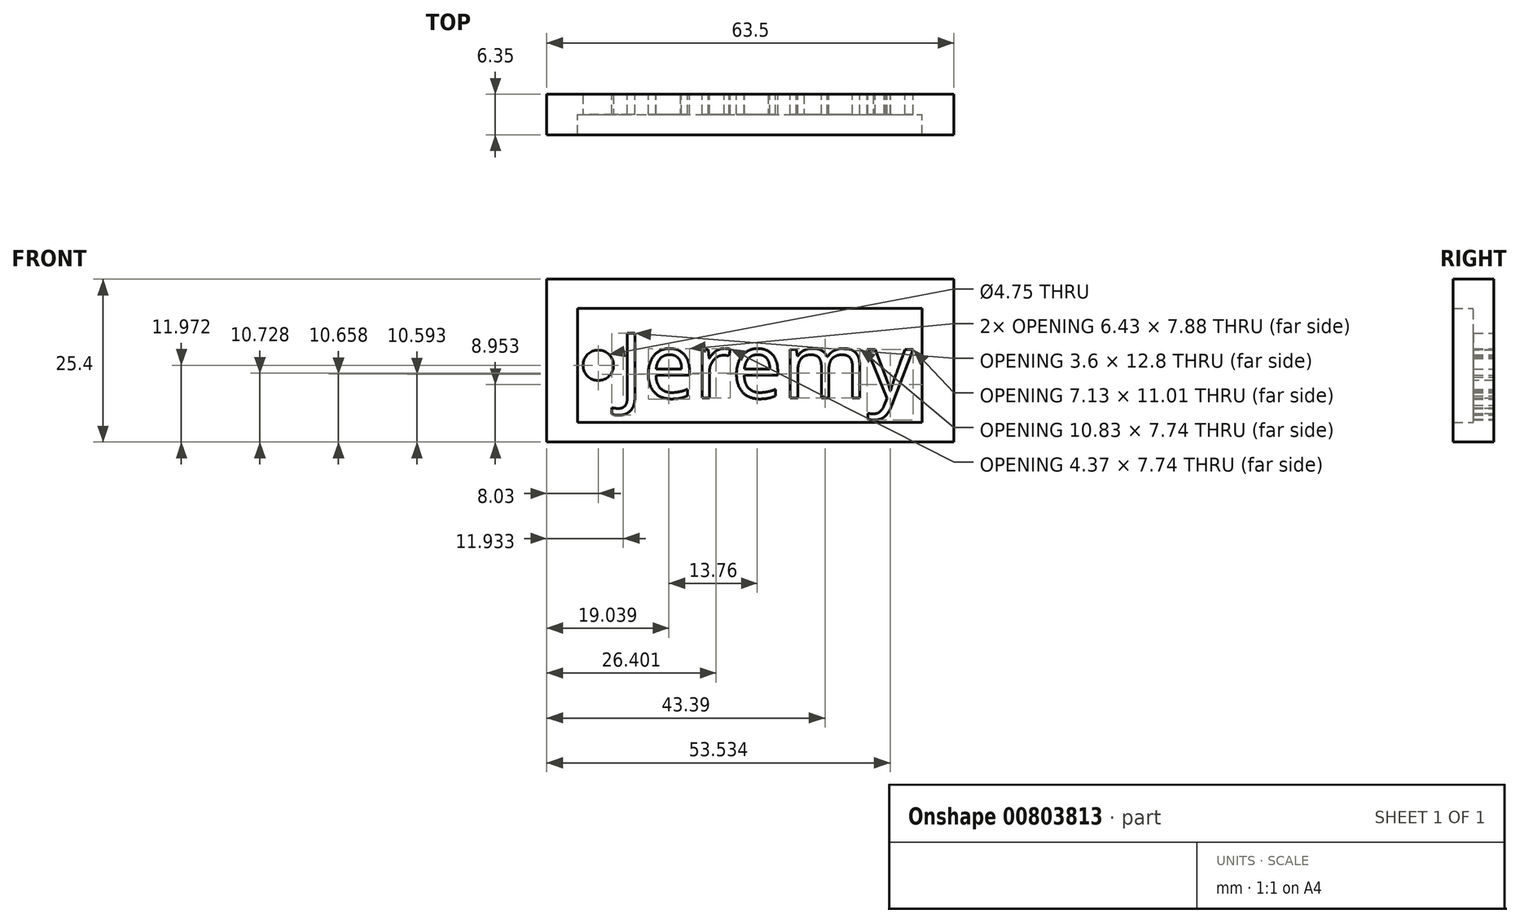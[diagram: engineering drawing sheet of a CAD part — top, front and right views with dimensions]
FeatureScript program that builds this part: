
annotation { "Feature Type Name" : "Feature", "Feature Type Description" : "" }
export const myFeature = defineFeature(function(context is Context, id is Id, definition is map)
    precondition{}
    {
        {
            var Q0;
            Q0=qCreatedBy(makeId("Front.planeOp"),FACE);
            var sketch = newSketch(context, id + "F0", { "sketchPlane" : qUnion([Q0])});
            skLineSegment(sketch, "E0.bottom", {"start": v(0, 0) * mm, "end": v(63.5, 0) * mm});
            skLineSegment(sketch, "E0.top", {"start": v(0, 25.4) * mm, "end": v(63.5, 25.4) * mm});
            skLineSegment(sketch, "E0.left", {"start": v(0, 0) * mm, "end": v(0, 25.4) * mm});
            skLineSegment(sketch, "E0.right", {"start": v(63.5, 0) * mm, "end": v(63.5, 25.4) * mm});
            skLineSegment(sketch, "E1.bottom", {"start": v(4.82, 3.07) * mm, "end": v(58.55, 3.07) * mm});
            skLineSegment(sketch, "E1.top", {"start": v(4.82, 20.88) * mm, "end": v(58.55, 20.88) * mm});
            skLineSegment(sketch, "E1.left", {"start": v(4.82, 3.07) * mm, "end": v(4.82, 20.88) * mm});
            skLineSegment(sketch, "E1.right", {"start": v(58.55, 3.07) * mm, "end": v(58.55, 20.88) * mm});
            skSolve(sketch);
        }
        {
            var Q0;
            Q0=makeQuery(id+"F0.imprint","IMPRINT",FACE,{"disambiguationData":[TD([[makeQuery(id+"F0.imprint","IMPRINT",EDGE,{"derivedFrom":sQuery(id+"F0.wireOp",EDGE,"E0.bottom")}),1.0]])]});
            extrude(context, id + "F1", {"entities" : qUnion([Q0]), "depth" : 6.35 * mm, "offsetDistance" : 25.4 * mm});
        }
        {
            var Q0;
            Q0=makeQuery(id+"F0.imprint","IMPRINT",FACE,{"disambiguationData":[TD([[makeQuery(id+"F0.imprint","IMPRINT",EDGE,{"derivedFrom":sQuery(id+"F0.wireOp",EDGE,"E1.bottom")}),1.0]])]});
            extrude(context, id + "F2", {"entities" : qUnion([Q0]), "operationType" : NewBodyOperationType.ADD, "depth" : 3.17 * mm, "offsetDistance" : 25.4 * mm});
        }
        {
            var Q0;
            Q0=makeQuery(id+"F2.opExtrude","CAP_FACE",FACE,{"disambiguationData":[OSD([sQuery(id+"F0.wireOp",EDGE,"E1.bottom"),sQuery(id+"F0.wireOp",EDGE,"E1.top"),sQuery(id+"F0.wireOp",EDGE,"E1.left"),sQuery(id+"F0.wireOp",EDGE,"E1.right")])],"isStart":false});
            var sketch = newSketch(context, id + "F3", { "sketchPlane" : qUnion([Q0])});
            skCircle(sketch, "E2", {"center": v(8.03, 11.97) * mm, "radius": 2.38 * mm});
            skPoint(sketch, "E2.centerSnap0", {"position": v(4.82, 11.97) * mm});
            skSolve(sketch);
        }
        {
            var Q0;
            Q0=makeQuery(id+"F3.imprint","IMPRINT",FACE,{"disambiguationData":[TD([[makeQuery(id+"F3.imprint","IMPRINT",EDGE,{"derivedFrom":sQuery(id+"F3.wireOp",EDGE,"E2")}),1.0]])]});
            extrude(context, id + "F4", {"entities" : qUnion([Q0]), "operationType" : NewBodyOperationType.REMOVE, "oppositeDirection" : true, "depth" : 3.17 * mm, "offsetDistance" : 25.4 * mm});
        }
        {
            var Q0;
            Q0=makeQuery(id+"F2.opExtrude","CAP_FACE",FACE,{"disambiguationData":[OSD([sQuery(id+"F0.wireOp",EDGE,"E1.bottom"),sQuery(id+"F0.wireOp",EDGE,"E1.top"),sQuery(id+"F0.wireOp",EDGE,"E1.left"),sQuery(id+"F0.wireOp",EDGE,"E1.right")])],"isStart":false});
            var sketch = newSketch(context, id + "F5", { "sketchPlane" : qUnion([Q0])});
            skText(sketch, "E3", { "text": "Jeremy", "fontName": "OpenSans-Regular.ttf"});
            const initialGuessF5  = {"E3": [0.01124, 0.00686, 1, 0, 0.01022]};
            skSetInitialGuess(sketch, initialGuessF5);
            skSolve(sketch);
        }
        {
            var Q0;
            Q0 = qSketchRegion(id + "F5", true);
            extrude(context, id + "F6", {"entities" : qUnion([Q0]), "operationType" : NewBodyOperationType.REMOVE, "depth" : 2.5 * mm, "offsetDistance" : 25.4 * mm, "hasSecondDirection" : true, "secondDirectionOppositeDirection" : true, "secondDirectionDepth" : 25.4 * mm});
        }
    });
